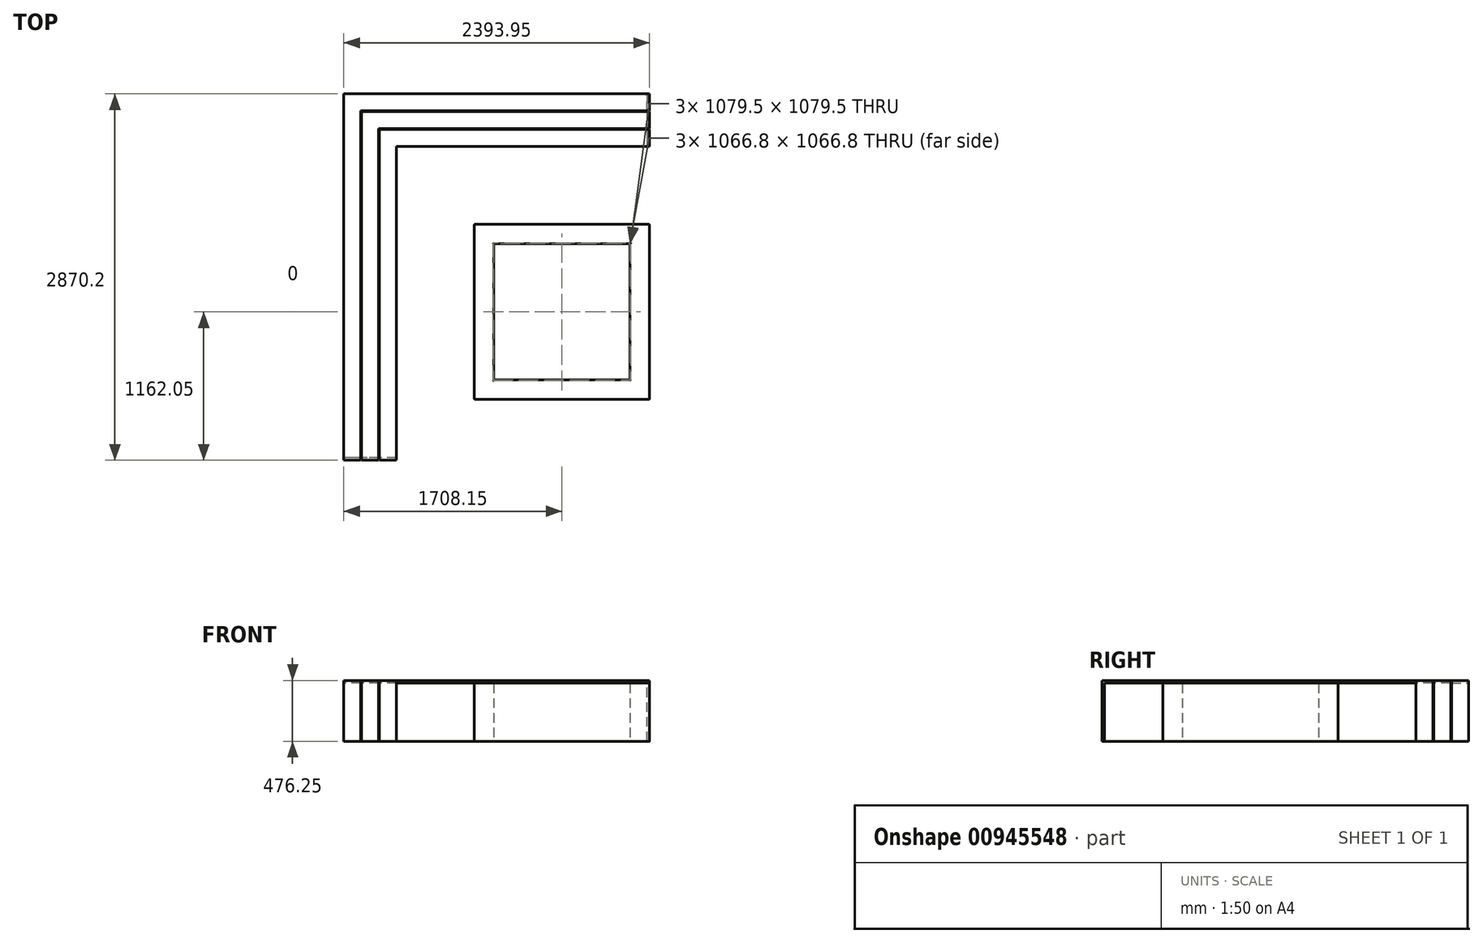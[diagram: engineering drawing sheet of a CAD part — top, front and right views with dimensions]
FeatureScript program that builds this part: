
annotation { "Feature Type Name" : "Feature", "Feature Type Description" : "" }
export const myFeature = defineFeature(function(context is Context, id is Id, definition is map)
    precondition{}
    {
        {
            var Q0;
            Q0=qCreatedBy(makeId("Top.planeOp"),FACE);
            var sketch = newSketch(context, id + "F0", { "sketchPlane" : qUnion([Q0])});
            skLineSegment(sketch, "E0.bottom", {"start": v(1270, 355.6) * mm, "end": v(203.2, 355.6) * mm});
            skLineSegment(sketch, "E0.top", {"start": v(1270, 1422.4) * mm, "end": v(203.2, 1422.4) * mm});
            skLineSegment(sketch, "E0.left", {"start": v(1270, 355.6) * mm, "end": v(1270, 1422.4) * mm});
            skLineSegment(sketch, "E0.right", {"start": v(203.2, 355.6) * mm, "end": v(203.2, 1422.4) * mm});
            skPoint(sketch, "E0.middle", {"position": v(736.6, 889) * mm});
            skLineSegment(sketch, "E1.bottom", {"start": v(1422.4, 203.2) * mm, "end": v(50.8, 203.2) * mm});
            skLineSegment(sketch, "E1.top", {"start": v(1422.4, 1574.8) * mm, "end": v(50.8, 1574.8) * mm});
            skLineSegment(sketch, "E1.left", {"start": v(1422.4, 203.2) * mm, "end": v(1422.4, 1574.8) * mm});
            skLineSegment(sketch, "E1.right", {"start": v(50.8, 203.2) * mm, "end": v(50.8, 1574.8) * mm});
            skLineSegment(sketch, "E2", {"start": v(50.8, 889) * mm, "end": v(203.2, 889) * mm, "construction": true});
            skSolve(sketch);
        }
        {
            var Q0;
            Q0=makeQuery(id+"F0.imprint","IMPRINT",FACE,{"disambiguationData":[TD([[makeQuery(id+"F0.imprint","IMPRINT",EDGE,{"derivedFrom":sQuery(id+"F0.wireOp",EDGE,"E0.bottom")}),1.0]])]});
            extrude(context, id + "F1", {"entities" : qUnion([Q0]), "depth" : 457.2 * mm, "offsetDistance" : 25.4 * mm});
        }
        {
            var Q0;
            Q0=makeQuery(id+"F1.opExtrude","CAP_EDGE",EDGE,{"disambiguationData":[OSD([sQuery(id+"F0.wireOp",EDGE,"E1.top")])],"isStart":false});
            var Q1;
            Q1=makeQuery(id+"F1.opExtrude","SWEPT_EDGE",EDGE,{"disambiguationData":[OSD([sQuery(id+"F0.wireOp",EDGE,"E1.top"),sQuery(id+"F0.wireOp",EDGE,"E1.left")])]});
            var Q2;
            Q2=makeQuery(id+"F1.opExtrude","CAP_EDGE",EDGE,{"disambiguationData":[OSD([sQuery(id+"F0.wireOp",EDGE,"E1.left")])],"isStart":false});
            var Q3;
            Q3=makeQuery(id+"F1.opExtrude","SWEPT_EDGE",EDGE,{"disambiguationData":[OSD([sQuery(id+"F0.wireOp",EDGE,"E1.top"),sQuery(id+"F0.wireOp",EDGE,"E1.right")])]});
            var Q4;
            Q4=makeQuery(id+"F1.opExtrude","CAP_EDGE",EDGE,{"disambiguationData":[OSD([sQuery(id+"F0.wireOp",EDGE,"E1.right")])],"isStart":false});
            var Q5;
            Q5=makeQuery(id+"F1.opExtrude","CAP_EDGE",EDGE,{"disambiguationData":[OSD([sQuery(id+"F0.wireOp",EDGE,"E0.right")])],"isStart":false});
            var Q6;
            Q6=makeQuery(id+"F1.opExtrude","CAP_EDGE",EDGE,{"disambiguationData":[OSD([sQuery(id+"F0.wireOp",EDGE,"E0.top")])],"isStart":false});
            var Q7;
            Q7=makeQuery(id+"F1.opExtrude","CAP_EDGE",EDGE,{"disambiguationData":[OSD([sQuery(id+"F0.wireOp",EDGE,"E0.left")])],"isStart":false});
            var Q8;
            Q8=makeQuery(id+"F1.opExtrude","CAP_EDGE",EDGE,{"disambiguationData":[OSD([sQuery(id+"F0.wireOp",EDGE,"E0.bottom")])],"isStart":false});
            var Q9;
            Q9=makeQuery(id+"F1.opExtrude","CAP_EDGE",EDGE,{"disambiguationData":[OSD([sQuery(id+"F0.wireOp",EDGE,"E1.bottom")])],"isStart":false});
            var Q10;
            Q10=makeQuery(id+"F1.opExtrude","SWEPT_EDGE",EDGE,{"disambiguationData":[OSD([sQuery(id+"F0.wireOp",EDGE,"E1.bottom"),sQuery(id+"F0.wireOp",EDGE,"E1.left")])]});
            var Q11;
            Q11=makeQuery(id+"F1.opExtrude","SWEPT_EDGE",EDGE,{"disambiguationData":[OSD([sQuery(id+"F0.wireOp",EDGE,"E1.bottom"),sQuery(id+"F0.wireOp",EDGE,"E1.right")])]});
            fillet(context, id + "F2", {"entities" : qUnion([Q0, Q1, Q2, Q3, Q4, Q5, Q6, Q7, Q8, Q9, Q10, Q11]), "radius" : 6.35 * mm, "tangentPropagation" : true, "allowEdgeOverflow" : false});
        }
        {
            var Q0;
            Q0=qCreatedBy(makeId("Top.planeOp"),FACE);
            var sketch = newSketch(context, id + "F3", { "sketchPlane" : qUnion([Q0])});
            skLineSegment(sketch, "E3", {"start": v(1403.35, 2184.4) * mm, "end": v(-558.8, 2184.4) * mm});
            skLineSegment(sketch, "E4", {"start": v(-558.8, 2184.4) * mm, "end": v(-558.8, -254) * mm});
            skLineSegment(sketch, "E5", {"start": v(-558.8, -254) * mm, "end": v(-971.55, -254) * mm});
            skLineSegment(sketch, "E6", {"start": v(-971.55, -254) * mm, "end": v(-971.55, 2597.15) * mm});
            skLineSegment(sketch, "E7", {"start": v(-971.55, 2597.15) * mm, "end": v(1403.35, 2597.15) * mm});
            skLineSegment(sketch, "E8", {"start": v(1403.35, 2597.15) * mm, "end": v(1403.35, 2184.4) * mm});
            skLineSegment(sketch, "E9", {"start": v(1403.35, 2184.4) * mm, "end": v(1422.4, 2184.4) * mm, "construction": true});
            skLineSegment(sketch, "E10", {"start": v(1422.4, 2184.4) * mm, "end": v(1422.4, 1574.8) * mm, "construction": true});
            skLineSegment(sketch, "E11", {"start": v(50.8, 203.2) * mm, "end": v(50.8, -254) * mm, "construction": true});
            skLineSegment(sketch, "E12", {"start": v(50.8, -254) * mm, "end": v(-558.8, -254) * mm});
            skSolve(sketch);
        }
        {
            var Q0;
            Q0=makeQuery(id+"F3.imprint","IMPRINT",FACE,{"disambiguationData":[TD([[makeQuery(id+"F3.imprint","IMPRINT",EDGE,{"derivedFrom":sQuery(id+"F3.wireOp",EDGE,"E3")}),-1.0]])]});
            extrude(context, id + "F4", {"entities" : qUnion([Q0]), "depth" : 457.2 * mm, "offsetDistance" : 25.4 * mm});
        }
        {
            var Q0;
            Q0=qCreatedBy(makeId("Top.planeOp"),FACE);
            var sketch = newSketch(context, id + "F5", { "sketchPlane" : qUnion([Q0])});
            skLineSegment(sketch, "E13.bottom", {"start": v(1403.35, 2184.4) * mm, "end": v(1422.4, 2184.4) * mm});
            skLineSegment(sketch, "E13.top", {"start": v(1403.35, 2317.75) * mm, "end": v(1422.4, 2317.75) * mm});
            skLineSegment(sketch, "E13.left", {"start": v(1403.35, 2184.4) * mm, "end": v(1403.35, 2317.75) * mm});
            skLineSegment(sketch, "E13.right", {"start": v(1422.4, 2184.4) * mm, "end": v(1422.4, 2317.75) * mm});
            skLineSegment(sketch, "E14.0.1.0", {"start": v(1403.35, 2324.1) * mm, "end": v(1422.4, 2324.1) * mm});
            skLineSegment(sketch, "E14.0.1.1", {"start": v(1422.4, 2324.1) * mm, "end": v(1422.4, 2457.45) * mm});
            skLineSegment(sketch, "E14.0.1.2", {"start": v(1403.35, 2457.45) * mm, "end": v(1422.4, 2457.45) * mm});
            skLineSegment(sketch, "E14.0.1.3", {"start": v(1403.35, 2324.1) * mm, "end": v(1403.35, 2457.45) * mm});
            skLineSegment(sketch, "E14.0.2.0", {"start": v(1403.35, 2463.8) * mm, "end": v(1422.4, 2463.8) * mm});
            skLineSegment(sketch, "E14.0.2.1", {"start": v(1422.4, 2463.8) * mm, "end": v(1422.4, 2597.15) * mm});
            skLineSegment(sketch, "E14.0.2.2", {"start": v(1403.35, 2597.15) * mm, "end": v(1422.4, 2597.15) * mm});
            skLineSegment(sketch, "E14.0.2.3", {"start": v(1403.35, 2463.8) * mm, "end": v(1403.35, 2597.15) * mm});
            skLineSegment(sketch, "E14.direction1", {"start": v(1403.35, 2184.4) * mm, "end": v(1400.81, 2184.4) * mm, "construction": true});
            skLineSegment(sketch, "E14.direction2", {"start": v(1403.35, 2184.4) * mm, "end": v(1403.35, 2324.1) * mm, "construction": true});
            skSolve(sketch);
        }
        {
            var Q0;
            Q0 = qSketchRegion(id + "F5", true);
            var Q1;
            Q1=makeQuery(id+"F4.opExtrude","SWEPT_EDGE",EDGE,{"disambiguationData":[OSD([sQuery(id+"F3.wireOp",EDGE,"E3"),sQuery(id+"F3.wireOp",EDGE,"E8")])]});
            var Q2;
            Q2=makeQuery(id+"F4.opExtrude","CAP_EDGE",EDGE,{"disambiguationData":[OSD([sQuery(id+"F3.wireOp",EDGE,"E3")])],"isStart":false});
            var Q3;
            Q3=makeQuery(id+"F4.opExtrude","CAP_EDGE",EDGE,{"disambiguationData":[OSD([sQuery(id+"F3.wireOp",EDGE,"E4")])],"isStart":false});
            var Q4;
            Q4=makeQuery(id+"F4.opExtrude","SWEPT_EDGE",EDGE,{"disambiguationData":[OSD([sQuery(id+"F3.wireOp",EDGE,"E4"),sQuery(id+"F3.wireOp",EDGE,"E5")])]});
            sweep(context, id + "F6", {"profiles" : qUnion([Q0]), "path" : qUnion([Q1, Q2, Q3, Q4])});
        }
    });
